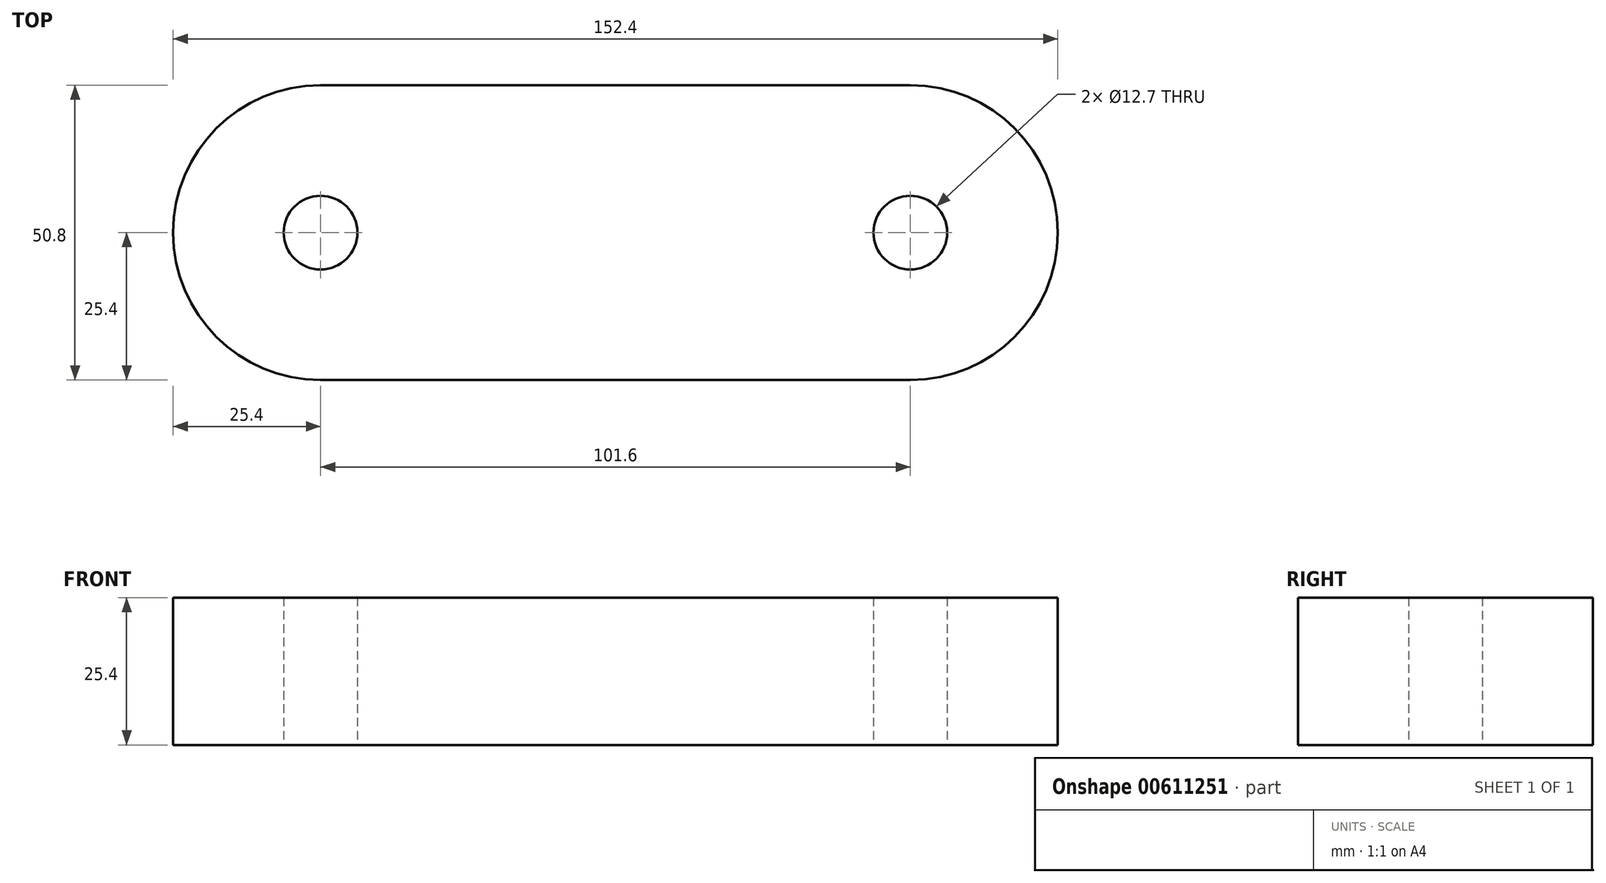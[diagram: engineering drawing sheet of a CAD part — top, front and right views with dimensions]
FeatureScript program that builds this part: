
annotation { "Feature Type Name" : "Feature", "Feature Type Description" : "" }
export const myFeature = defineFeature(function(context is Context, id is Id, definition is map)
    precondition{}
    {
        {
            var Q0;
            Q0=qCreatedBy(makeId("Top.planeOp"),FACE);
            var sketch = newSketch(context, id + "F0", { "sketchPlane" : qUnion([Q0])});
            skLineSegment(sketch, "E0.bottom", {"start": v(50.8, -25.4) * mm, "end": v(-50.8, -25.4) * mm});
            skLineSegment(sketch, "E0.top", {"start": v(50.8, 25.4) * mm, "end": v(-50.8, 25.4) * mm});
            skLineSegment(sketch, "E0.left", {"start": v(50.8, -25.4) * mm, "end": v(50.8, 25.4) * mm});
            skLineSegment(sketch, "E0.right", {"start": v(-50.8, -25.4) * mm, "end": v(-50.8, 25.4) * mm});
            skPoint(sketch, "E0.middle", {"position": v(0, 0) * mm});
            skArc(sketch, "E1", {"start": v(50.8, -25.4) * mm, "mid": v(76.2, 0) * mm, "end": v(50.8, 25.4) * mm});
            skArc(sketch, "E2", {"start": v(-50.8, 25.4) * mm, "mid": v(-76.2, 0) * mm, "end": v(-50.8, -25.4) * mm});
            skCircle(sketch, "E3", {"center": v(-50.8, 0) * mm, "radius": 6.35 * mm});
            skCircle(sketch, "E4", {"center": v(50.8, 0) * mm, "radius": 6.35 * mm});
            skSolve(sketch);
        }
        {
            var Q0;
            {var subQ5=sQuery(id+"F0.wireOp",EDGE,"E0.bottom");Q0=makeQuery(id+"F0.imprint","IMPRINT",FACE,{"disambiguationData":[TD([[makeQuery(id+"F0.imprint","IMPRINT",EDGE,{"derivedFrom":subQ5}),-1.0]])]});}
            var Q1;
            {var subQ0=sQuery(id+"F0.wireOp",EDGE,"E1");Q1=makeQuery(id+"F0.imprint","IMPRINT",FACE,{"disambiguationData":[TD([[makeQuery(id+"F0.imprint","IMPRINT",EDGE,{"derivedFrom":subQ0}),1.0]])]});}
            var Q2;
            {var subQ0=sQuery(id+"F0.wireOp",EDGE,"E2");Q2=makeQuery(id+"F0.imprint","IMPRINT",FACE,{"disambiguationData":[TD([[makeQuery(id+"F0.imprint","IMPRINT",EDGE,{"derivedFrom":subQ0}),1.0]])]});}
            extrude(context, id + "F1", {"entities" : qUnion([Q0, Q1, Q2]), "depth" : 25.4 * mm, "offsetDistance" : 25.4 * mm});
        }
    });
